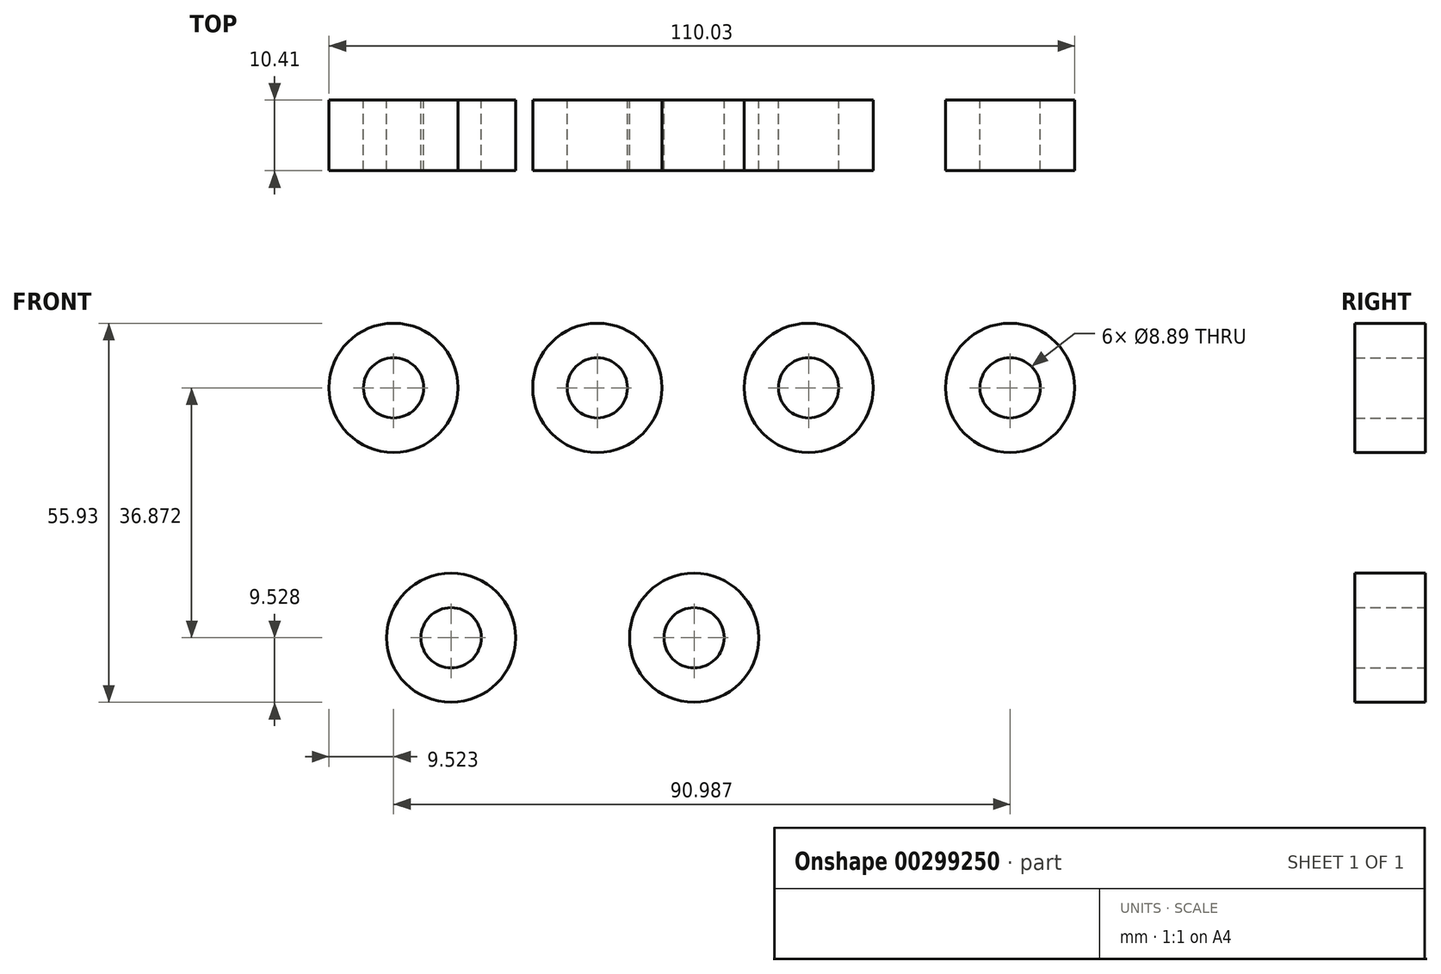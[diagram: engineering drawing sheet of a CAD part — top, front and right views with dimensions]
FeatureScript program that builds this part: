
annotation { "Feature Type Name" : "Feature", "Feature Type Description" : "" }
export const myFeature = defineFeature(function(context is Context, id is Id, definition is map)
    precondition{}
    {
        {
            var Q0;
            Q0=qCreatedBy(makeId("Front.planeOp"),FACE);
            var sketch = newSketch(context, id + "F0", { "sketchPlane" : qUnion([Q0])});
            skCircle(sketch, "E0", {"center": v(-39.69, 0) * mm, "radius": 4.45 * mm});
            skCircle(sketch, "E1", {"center": v(-39.69, 0) * mm, "radius": 9.53 * mm});
            skCircle(sketch, "E2", {"center": v(-9.62, 0) * mm, "radius": 4.45 * mm});
            skCircle(sketch, "E3", {"center": v(-9.62, 0) * mm, "radius": 9.53 * mm});
            skCircle(sketch, "E4", {"center": v(21.57, 0) * mm, "radius": 4.45 * mm});
            skCircle(sketch, "E5", {"center": v(21.57, 0) * mm, "radius": 9.53 * mm});
            skCircle(sketch, "E6", {"center": v(51.3, 0) * mm, "radius": 4.45 * mm});
            skCircle(sketch, "E7", {"center": v(51.3, 0) * mm, "radius": 9.53 * mm});
            skCircle(sketch, "E8", {"center": v(-31.19, -36.87) * mm, "radius": 4.45 * mm});
            skCircle(sketch, "E9", {"center": v(-31.19, -36.87) * mm, "radius": 9.53 * mm});
            skCircle(sketch, "E10", {"center": v(4.66, -36.87) * mm, "radius": 4.45 * mm});
            skCircle(sketch, "E11", {"center": v(4.66, -36.87) * mm, "radius": 9.53 * mm});
            skSolve(sketch);
        }
        {
            var Q0;
            Q0 = qSketchRegion(id + "F0", true);
            extrude(context, id + "F1", {"entities" : qUnion([Q0]), "depth" : 10.4 * mm});
        }
    });
